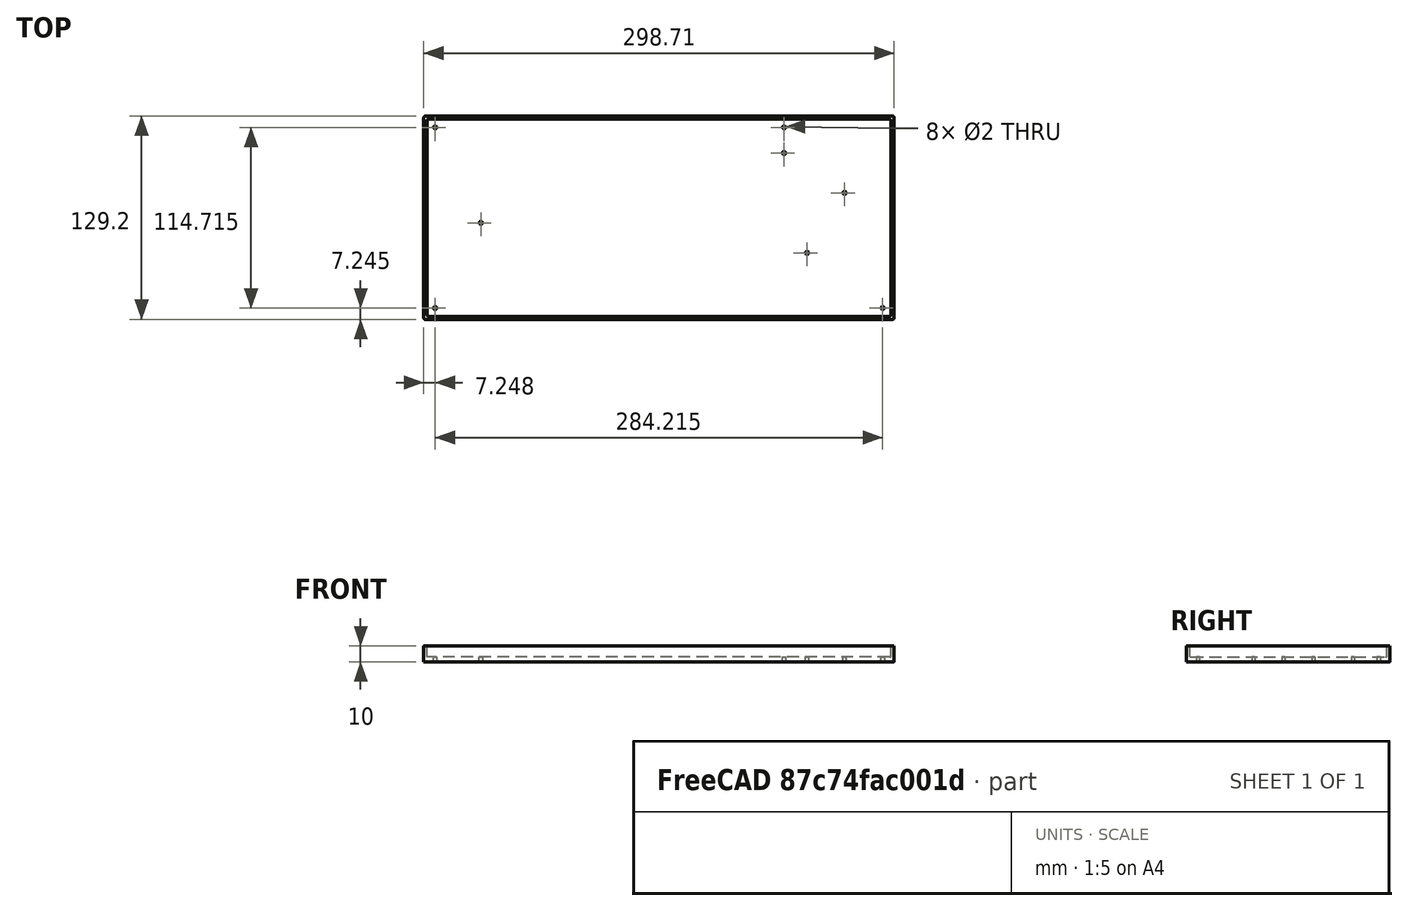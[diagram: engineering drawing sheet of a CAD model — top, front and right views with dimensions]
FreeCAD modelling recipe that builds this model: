
FCSTD DOCUMENT  (FreeCAD 0.18R4 (GitTag))
Label: CaseBase
License: All rights reserved
LicenseURL: http://en.wikipedia.org/wiki/All_rights_reserved
objects: Part::Feature×24, Part::Extrusion×10, Part::Cut×9, Part::FeaturePython×2
note: 45 computed .brp shape members not serialized (recipe doc carries the construction recipe); baked Part::Feature solids carry a one-line shape summary decoded from their .brp

FEATURE [Part::Feature] Shape
  shape: bbox 1 x 1 x 2e-07 mm, 0 faces, 0 solids (baked)
FEATURE [Part::Feature] Shape001
  shape: bbox 1 x 1 x 2e-07 mm, 0 faces, 0 solids (baked)
FEATURE [Part::Feature] Shape002
  shape: bbox 2e-07 x 123.2 x 2e-07 mm, 0 faces, 0 solids (baked)
FEATURE [Part::Feature] Shape003
  shape: bbox 1 x 1 x 2e-07 mm, 0 faces, 0 solids (baked)
FEATURE [Part::Feature] Shape004
  shape: bbox 2e-07 x 127.2 x 2e-07 mm, 0 faces, 0 solids (baked)
FEATURE [Part::Feature] Shape005
  shape: bbox 1 x 1 x 2e-07 mm, 0 faces, 0 solids (baked)
FEATURE [Part::Feature] Shape006
  shape: bbox 292.7 x 2e-07 x 2e-07 mm, 0 faces, 0 solids (baked)
FEATURE [Part::Feature] Shape007
  shape: bbox 1 x 1 x 2e-07 mm, 0 faces, 0 solids (baked)
FEATURE [Part::Feature] Shape008
  shape: bbox 296.7 x 2e-07 x 2e-07 mm, 0 faces, 0 solids (baked)
FEATURE [Part::Feature] Shape009
  shape: bbox 1 x 1 x 2e-07 mm, 0 faces, 0 solids (baked)
FEATURE [Part::Feature] Shape010
  shape: bbox 2e-07 x 123.2 x 2e-07 mm, 0 faces, 0 solids (baked)
FEATURE [Part::Feature] Shape011
  shape: bbox 292.7 x 2e-07 x 2e-07 mm, 0 faces, 0 solids (baked)
FEATURE [Part::Feature] Shape012
  shape: bbox 1 x 1 x 2e-07 mm, 0 faces, 0 solids (baked)
FEATURE [Part::Feature] Shape013
  shape: bbox 2e-07 x 127.2 x 2e-07 mm, 0 faces, 0 solids (baked)
FEATURE [Part::Feature] Shape014
  shape: bbox 296.7 x 2e-07 x 2e-07 mm, 0 faces, 0 solids (baked)
FEATURE [Part::Feature] Shape015
  shape: bbox 1 x 1 x 2e-07 mm, 0 faces, 0 solids (baked)
FEATURE [Part::Feature] Shape016 .. Shape023  x8 (patterned run collapsed; names and placements below)
  shape: bbox 2 x 2 x 2e-07 mm, 0 faces, 0 solids (baked)
FEATURE [Part::FeaturePython] Connect  # WARN: FeaturePython — macro-defined, semantics opaque (R4)
  Objects = -> [Shape001,Shape014,Shape015,Shape013,Shape009,Shape008,Shape005,Shape004]
  Tolerance = 0
FEATURE [Part::FeaturePython] Connect001  # WARN: FeaturePython — macro-defined, semantics opaque (R4)
  Objects = -> [Shape,Shape011,Shape002,Shape012,Shape010,Shape007,Shape006,Shape003]
  Tolerance = 0
FEATURE [Part::Extrusion] Extrude
  Base = -> Shape016
  Dir = (0,0,1)
  DirMode = 0
  FaceMakerClass = Part::FaceMakerBullseye
  LengthFwd = 10
  LengthRev = 0
  Solid = true
  Symmetric = false
FEATURE [Part::Extrusion] Extrude001
  Base = -> Shape017
  Dir = (0,0,1)
  DirMode = 0
  FaceMakerClass = Part::FaceMakerBullseye
  LengthFwd = 10
  LengthRev = 0
  Solid = true
  Symmetric = false
FEATURE [Part::Extrusion] Extrude002
  Base = -> Shape018
  Dir = (0,0,1)
  DirMode = 0
  FaceMakerClass = Part::FaceMakerBullseye
  LengthFwd = 10
  LengthRev = 0
  Solid = true
  Symmetric = false
FEATURE [Part::Extrusion] Extrude003
  Base = -> Shape019
  Dir = (0,0,1)
  DirMode = 0
  FaceMakerClass = Part::FaceMakerBullseye
  LengthFwd = 10
  LengthRev = 0
  Solid = true
  Symmetric = false
FEATURE [Part::Extrusion] Extrude004
  Base = -> Shape020
  Dir = (0,0,1)
  DirMode = 0
  FaceMakerClass = Part::FaceMakerBullseye
  LengthFwd = 10
  LengthRev = 0
  Solid = true
  Symmetric = false
FEATURE [Part::Extrusion] Extrude005
  Base = -> Shape021
  Dir = (0,0,1)
  DirMode = 0
  FaceMakerClass = Part::FaceMakerBullseye
  LengthFwd = 10
  LengthRev = 0
  Solid = true
  Symmetric = false
FEATURE [Part::Extrusion] Extrude006
  Base = -> Shape022
  Dir = (0,0,1)
  DirMode = 0
  FaceMakerClass = Part::FaceMakerBullseye
  LengthFwd = 10
  LengthRev = 0
  Solid = true
  Symmetric = false
FEATURE [Part::Extrusion] Extrude007
  Base = -> Shape023
  Dir = (0,0,1)
  DirMode = 0
  FaceMakerClass = Part::FaceMakerBullseye
  LengthFwd = 10
  LengthRev = 0
  Solid = true
  Symmetric = false
FEATURE [Part::Extrusion] Extrude008
  Base = -> Connect
  Dir = (0,0,1)
  DirMode = 0
  FaceMakerClass = Part::FaceMakerBullseye
  LengthFwd = 10
  LengthRev = 0
  Solid = true
  Symmetric = false
FEATURE [Part::Extrusion] Extrude009
  Base = -> Connect001
  Dir = (0,0,1)
  DirMode = 0
  FaceMakerClass = Part::FaceMakerBullseye
  LengthFwd = 10
  LengthRev = 0
  Placement = pos=(0,0,3) rot=(0,0,1;0rad)
  Solid = true
  Symmetric = false
FEATURE [Part::Cut] Cut
  Base = -> Extrude008
  Tool = -> Extrude
FEATURE [Part::Cut] Cut001
  Base = -> Cut
  Tool = -> Extrude001
FEATURE [Part::Cut] Cut002
  Base = -> Cut001
  Tool = -> Extrude002
FEATURE [Part::Cut] Cut003
  Base = -> Cut002
  Tool = -> Extrude003
FEATURE [Part::Cut] Cut004
  Base = -> Cut003
  Tool = -> Extrude004
FEATURE [Part::Cut] Cut005
  Base = -> Cut004
  Tool = -> Extrude005
FEATURE [Part::Cut] Cut006
  Base = -> Cut005
  Tool = -> Extrude006
FEATURE [Part::Cut] Cut007
  Base = -> Cut006
  Tool = -> Extrude007
FEATURE [Part::Cut] Cut008
  Base = -> Cut007
  Tool = -> Extrude009
